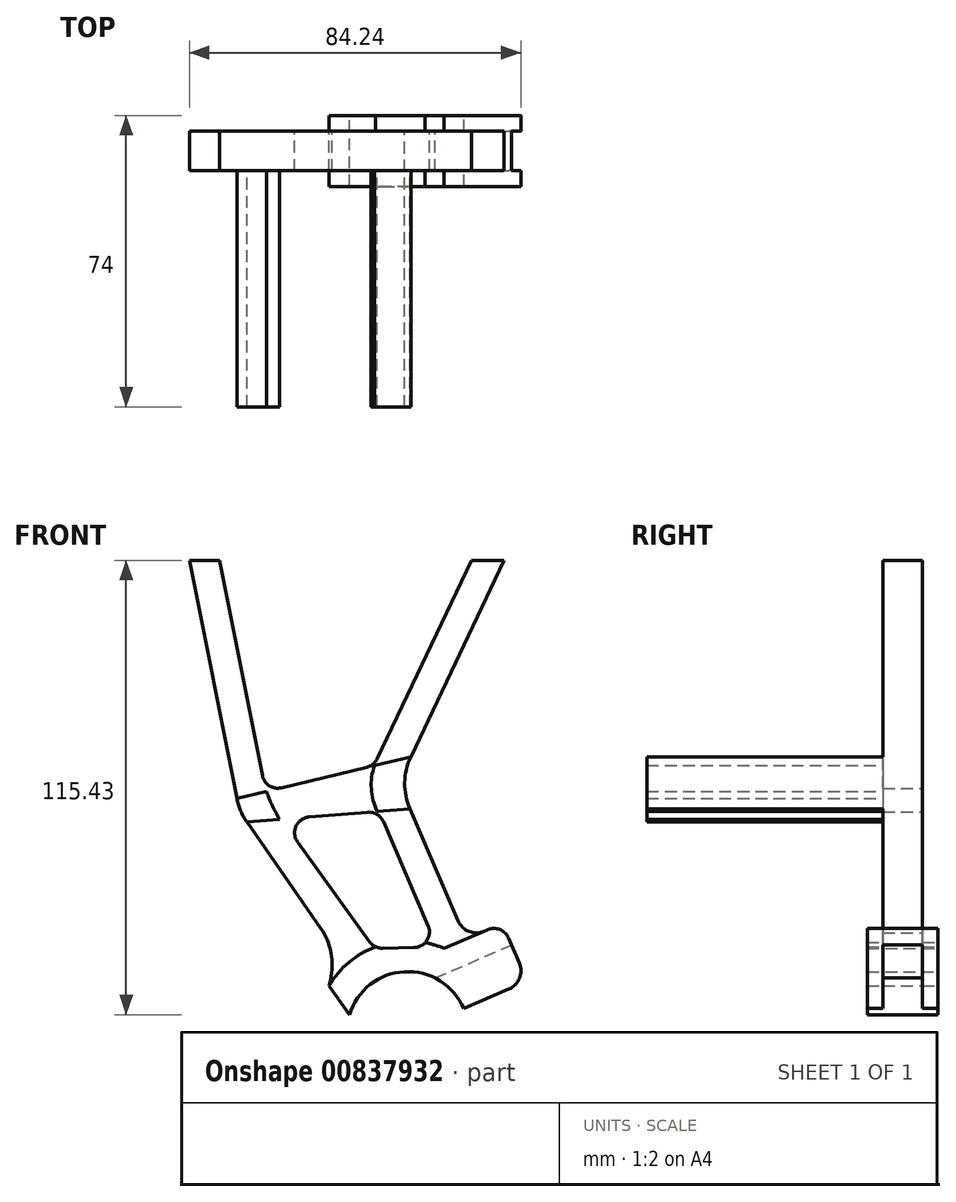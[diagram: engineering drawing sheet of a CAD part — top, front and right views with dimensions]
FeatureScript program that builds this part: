
annotation { "Feature Type Name" : "Feature", "Feature Type Description" : "" }
export const myFeature = defineFeature(function(context is Context, id is Id, definition is map)
    precondition{}
    {
        {
            var Q0;
            Q0=qCreatedBy(makeId("Front.planeOp"),FACE);
            var sketch = newSketch(context, id + "F0", { "sketchPlane" : qUnion([Q0])});
            skCircle(sketch, "E0", {"center": v(15.5, -66) * mm, "radius": 15.5 * mm});
            skLineSegment(sketch, "E1.bottom", {"start": v(-80, 54) * mm, "end": v(80, 54) * mm});
            skLineSegment(sketch, "E1.top", {"start": v(-80, 60) * mm, "end": v(80, 60) * mm});
            skLineSegment(sketch, "E1.left", {"start": v(-80, 54) * mm, "end": v(-80, 60) * mm});
            skLineSegment(sketch, "E1.right", {"start": v(80, 54) * mm, "end": v(80, 60) * mm});
            skLineSegment(sketch, "E2", {"start": v(-40, 54) * mm, "end": v(-27.92, -6.51) * mm});
            skCircle(sketch, "E3", {"center": v(15.5, -66) * mm, "radius": 23 * mm});
            skLineSegment(sketch, "E4", {"start": v(-25.36, -12.5) * mm, "end": v(-6.56, -39.57) * mm});
            skLineSegment(sketch, "E5", {"start": v(40, 54) * mm, "end": v(16.28, 4.1) * mm});
            skLineSegment(sketch, "E6", {"start": v(16.03, -9.1) * mm, "end": v(36.62, -56.9) * mm});
            skPoint(sketch, "E7.visualSharp", {"position": v(13.17, -2.45) * mm});
            skArc(sketch, "E7.filletArc", {"start": v(16.28, 4.1) * mm, "mid": v(14.73, -2.48) * mm, "end": v(16.03, -9.1) * mm});
            skPoint(sketch, "E8.visualSharp", {"position": v(-27.26, -9.77) * mm});
            skArc(sketch, "E8.filletArc", {"start": v(-27.92, -6.51) * mm, "mid": v(-26.95, -9.64) * mm, "end": v(-25.36, -12.5) * mm});
            skLineSegment(sketch, "E9", {"start": v(-16.58, -3.79) * mm, "end": v(5.05, 1.4) * mm});
            skLineSegment(sketch, "E10", {"start": v(-9.57, -11.2) * mm, "end": v(5.28, -9.99) * mm});
            skLineSegment(sketch, "E11", {"start": v(-32.35, 54) * mm, "end": v(-21.43, -0.68) * mm});
            skLineSegment(sketch, "E12", {"start": v(-12.49, -17.54) * mm, "end": v(5.82, -42.9) * mm});
            skLineSegment(sketch, "E13", {"start": v(31.7, 54) * mm, "end": v(7.73, 3.57) * mm});
            skLineSegment(sketch, "E14", {"start": v(9.28, -12.4) * mm, "end": v(20.66, -38.8) * mm});
            skArc(sketch, "E15.filletArc", {"start": v(-9.57, -11.2) * mm, "mid": v(-12.88, -13.52) * mm, "end": v(-12.49, -17.54) * mm});
            skArc(sketch, "E16.filletArc", {"start": v(9.28, -12.4) * mm, "mid": v(7.67, -10.55) * mm, "end": v(5.28, -9.99) * mm});
            skArc(sketch, "E17.filletArc", {"start": v(5.05, 1.4) * mm, "mid": v(6.63, 2.18) * mm, "end": v(7.73, 3.57) * mm});
            skArc(sketch, "E18.filletArc", {"start": v(-21.43, -0.68) * mm, "mid": v(-19.66, -3.27) * mm, "end": v(-16.58, -3.79) * mm});
            skLineSegment(sketch, "E19", {"start": v(9.15, -44.56) * mm, "end": v(17.08, -44.4) * mm});
            skPoint(sketch, "E20.visualSharp", {"position": v(7.05, -44.6) * mm});
            skArc(sketch, "E20.filletArc", {"start": v(5.82, -42.9) * mm, "mid": v(7.28, -44.15) * mm, "end": v(9.15, -44.56) * mm});
            skPoint(sketch, "E21.visualSharp", {"position": v(23.01, -44.26) * mm});
            skArc(sketch, "E21.filletArc", {"start": v(17.08, -44.4) * mm, "mid": v(20.36, -42.55) * mm, "end": v(20.66, -38.8) * mm});
            skLineSegment(sketch, "E22", {"start": v(2.52, -63.97) * mm, "end": v(-12.93, -42.55) * mm});
            skPoint(sketch, "E22.endSnap0", {"position": v(20.36, -42.55) * mm});
            skLineSegment(sketch, "E23", {"start": v(-8.28, -49) * mm, "end": v(3.89, -40.23) * mm});
            skLineSegment(sketch, "E24", {"start": v(-7.5, -66) * mm, "end": v(-4.16, -52.56) * mm});
            skPoint(sketch, "E25.newPointA", {"position": v(-2.2, -44.62) * mm});
            skPoint(sketch, "E25.newPointB", {"position": v(0, -49) * mm});
            skArc(sketch, "E25.filletArc", {"start": v(-4.16, -52.56) * mm, "mid": v(-3.96, -45.8) * mm, "end": v(-6.56, -39.57) * mm});
            skLineSegment(sketch, "E26", {"start": v(15.5, -66) * mm, "end": v(36.62, -56.9) * mm});
            skLineSegment(sketch, "E27", {"start": v(36.62, -56.9) * mm, "end": v(45.8, -52.94) * mm});
            skLineSegment(sketch, "E28", {"start": v(45.8, -52.94) * mm, "end": v(39.48, -38.25) * mm});
            skLineSegment(sketch, "E29", {"start": v(39.48, -38.25) * mm, "end": v(-3.82, -56.9) * mm});
            skSolve(sketch);
        }
        {
            var Q0;
            {var subQ5=sQuery(id+"F0.wireOp",EDGE,"E2");Q0=makeQuery(id+"F0.imprint","IMPRINT",FACE,{"disambiguationData":[TD([[makeQuery(id+"F0.imprint","IMPRINT",EDGE,{"derivedFrom":subQ5}),1.0]])]});}
            var Q1;
            {var subQ9=sQuery(id+"F0.wireOp",EDGE,"E19");Q1=makeQuery(id+"F0.imprint","IMPRINT",FACE,{"disambiguationData":[TD([[makeQuery(id+"F0.imprint","IMPRINT",EDGE,{"derivedFrom":subQ9}),-1.0]])]});}
            var Q2;
            {var subQ3=sQuery(id+"F0.wireOp",EDGE,"E3");var subQ5=sQuery(id+"F0.wireOp",EDGE,"E20.filletArc");var subQ8=makeQuery(id+"F0.imprint","INTERSECT",VERTEX,{"derivedFrom":[subQ3,subQ5]});Q2=makeQuery(id+"F0.imprint","IMPRINT",FACE,{"disambiguationData":[TD([[makeQuery(id+"F0.imprint","IMPRINT",EDGE,{"disambiguationData":[TD([[subQ8,-1.0]])],"derivedFrom":subQ3}),-1.0]])]});}
            var Q3;
            {var subQ0=sQuery(id+"F0.wireOp",EDGE,"E27");Q3=makeQuery(id+"F0.imprint","IMPRINT",FACE,{"disambiguationData":[TD([[makeQuery(id+"F0.imprint","IMPRINT",EDGE,{"derivedFrom":subQ0}),1.0]])]});}
            var Q4;
            {var subQ0=sQuery(id+"F0.wireOp",EDGE,"E29");var subQ1=sQuery(id+"F0.wireOp",EDGE,"E0");var subQ2=makeQuery(id+"F0.imprint","INTERSECT",VERTEX,{"derivedFrom":[subQ1,subQ0]});Q4=makeQuery(id+"F0.imprint","IMPRINT",FACE,{"disambiguationData":[TD([[makeQuery(id+"F0.imprint","IMPRINT",EDGE,{"disambiguationData":[TD([[subQ2,1.0]])],"derivedFrom":subQ1}),-1.0]])]});}
            var Q5;
            {var subQ0=sQuery(id+"F0.wireOp",EDGE,"E6");var subQ3=sQuery(id+"F0.wireOp",EDGE,"E29");var subQ5=makeQuery(id+"F0.imprint","INTERSECT",VERTEX,{"derivedFrom":[subQ0,subQ3]});Q5=makeQuery(id+"F0.imprint","IMPRINT",FACE,{"disambiguationData":[TD([[makeQuery(id+"F0.imprint","IMPRINT",EDGE,{"disambiguationData":[TD([[subQ5,-1.0]])],"derivedFrom":subQ3}),1.0]])]});}
            extrude(context, id + "F1", {"entities" : qUnion([Q0, Q1, Q2, Q3, Q4, Q5]), "depth" : 10 * mm, "offsetDistance" : 25 * mm});
        }
        {
            var Q0;
            Q0=makeQuery(id+"F1.opExtrude","CAP_FACE",FACE,{"disambiguationData":[OSD([sQuery(id+"F0.wireOp",EDGE,"E0"),sQuery(id+"F0.wireOp",EDGE,"E1.bottom"),sQuery(id+"F0.wireOp",EDGE,"E2"),sQuery(id+"F0.wireOp",EDGE,"E4"),sQuery(id+"F0.wireOp",EDGE,"E5"),sQuery(id+"F0.wireOp",EDGE,"E6"),sQuery(id+"F0.wireOp",EDGE,"E7.filletArc"),sQuery(id+"F0.wireOp",EDGE,"E8.filletArc"),sQuery(id+"F0.wireOp",EDGE,"E9"),sQuery(id+"F0.wireOp",EDGE,"E10"),sQuery(id+"F0.wireOp",EDGE,"E11"),sQuery(id+"F0.wireOp",EDGE,"E12"),sQuery(id+"F0.wireOp",EDGE,"E13"),sQuery(id+"F0.wireOp",EDGE,"E14"),sQuery(id+"F0.wireOp",EDGE,"E15.filletArc"),sQuery(id+"F0.wireOp",EDGE,"E16.filletArc"),sQuery(id+"F0.wireOp",EDGE,"E17.filletArc"),sQuery(id+"F0.wireOp",EDGE,"E18.filletArc"),sQuery(id+"F0.wireOp",EDGE,"E19"),sQuery(id+"F0.wireOp",EDGE,"E20.filletArc"),sQuery(id+"F0.wireOp",EDGE,"E21.filletArc"),sQuery(id+"F0.wireOp",EDGE,"E22"),sQuery(id+"F0.wireOp",EDGE,"E24"),sQuery(id+"F0.wireOp",EDGE,"E25.filletArc"),sQuery(id+"F0.wireOp",EDGE,"E26"),sQuery(id+"F0.wireOp",EDGE,"E27"),sQuery(id+"F0.wireOp",EDGE,"E28"),sQuery(id+"F0.wireOp",EDGE,"E29")])],"isStart":false});
            var sketch = newSketch(context, id + "F2", { "sketchPlane" : qUnion([Q0])});
            skLineSegment(sketch, "E30", {"start": v(39.48, -38.25) * mm, "end": v(45.8, -52.94) * mm});
            skLineSegment(sketch, "E31", {"start": v(45.8, -52.94) * mm, "end": v(29.74, -59.87) * mm});
            skArc(sketch, "E32", {"start": v(29.74, -59.87) * mm, "mid": v(14.67, -50.52) * mm, "end": v(0.69, -61.43) * mm});
            skCircle(sketch, "E33", {"center": v(15.5, -66) * mm, "radius": 23.3 * mm});
            skLineSegment(sketch, "E34", {"start": v(0.69, -61.43) * mm, "end": v(-4.56, -54.16) * mm});
            skLineSegment(sketch, "E35", {"start": v(39.48, -38.25) * mm, "end": v(24.72, -44.6) * mm});
            skSolve(sketch);
        }
        {
            var Q0;
            {var subQ6=sQuery(id+"F2.wireOp",EDGE,"E32");Q0=makeQuery(id+"F2.imprint","IMPRINT",FACE,{"disambiguationData":[TD([[makeQuery(id+"F2.imprint","IMPRINT",EDGE,{"derivedFrom":subQ6}),-1.0]])]});}
            var Q1;
            {var subQ5=sQuery(id+"F2.wireOp",EDGE,"E30");Q1=makeQuery(id+"F2.imprint","IMPRINT",FACE,{"disambiguationData":[TD([[makeQuery(id+"F2.imprint","IMPRINT",EDGE,{"derivedFrom":subQ5}),1.0]])]});}
            extrude(context, id + "F3", {"entities" : qUnion([Q0, Q1]), "operationType" : NewBodyOperationType.ADD, "depth" : 4 * mm, "offsetDistance" : 25 * mm, "hasSecondDirection" : true, "secondDirectionOppositeDirection" : true, "secondDirectionDepth" : 14 * mm});
        }
        {
            var Q0;
            Q0=makeQuery(id+"F3.boolean.opBoolean","MERGE",FACE,{"derivedFrom":[makeQuery(id+"F1.opExtrude","SWEPT_FACE",FACE,{"disambiguationData":[OSD([sQuery(id+"F0.wireOp",EDGE,"E28")])]}),makeQuery(id+"F3.opExtrude","SWEPT_FACE",FACE,{"disambiguationData":[OSD([sQuery(id+"F2.wireOp",EDGE,"E30")])]})]});
            var sketch = newSketch(context, id + "F4", { "sketchPlane" : qUnion([Q0])});
            skLineSegment(sketch, "E36.bottom", {"start": v(-10, -66.75) * mm, "end": v(0, -66.75) * mm});
            skLineSegment(sketch, "E36.top", {"start": v(-10, -56.75) * mm, "end": v(0, -56.75) * mm});
            skLineSegment(sketch, "E36.left", {"start": v(-10, -66.75) * mm, "end": v(-10, -56.75) * mm});
            skLineSegment(sketch, "E36.right", {"start": v(0, -66.75) * mm, "end": v(0, -56.75) * mm});
            skSolve(sketch);
        }
        {
            var Q0;
            Q0=makeQuery(id+"F4.imprint","IMPRINT",FACE,{"disambiguationData":[TD([[makeQuery(id+"F4.imprint","IMPRINT",EDGE,{"derivedFrom":sQuery(id+"F4.wireOp",EDGE,"E36.bottom")}),1.0]])]});
            extrude(context, id + "F5", {"entities" : qUnion([Q0]), "operationType" : NewBodyOperationType.REMOVE, "oppositeDirection" : true, "depth" : 25 * mm, "offsetDistance" : 25 * mm});
        }
        {
            var Q0;
            Q0=makeQuery(id+"F1.opExtrude","SWEPT_EDGE",EDGE,{"disambiguationData":[OSD([sQuery(id+"F0.wireOp",EDGE,"E6"),sQuery(id+"F0.wireOp",EDGE,"E29")])]});
            fillet(context, id + "F6", {"entities" : qUnion([Q0]), "radius" : 5 * mm, "tangentPropagation" : true, "allowEdgeOverflow" : false});
        }
        {
            var Q0;
            Q0=makeQuery(id+"F3.boolean.opBoolean","MERGE",EDGE,{"derivedFrom":[makeQuery(id+"F1.opExtrude","SWEPT_EDGE",EDGE,{"disambiguationData":[OSD([sQuery(id+"F0.wireOp",EDGE,"E28"),sQuery(id+"F0.wireOp",EDGE,"E29")])]}),makeQuery(id+"F3.opExtrude","SWEPT_EDGE",EDGE,{"disambiguationData":[OSD([sQuery(id+"F2.wireOp",EDGE,"E30"),sQuery(id+"F2.wireOp",EDGE,"E35")])]})]});
            fillet(context, id + "F7", {"entities" : qUnion([Q0]), "radius" : 4 * mm, "tangentPropagation" : true, "allowEdgeOverflow" : false});
        }
        {
            var Q0;
            {var subQ0=sQuery(id+"F2.wireOp",EDGE,"E31");var subQ1=sQuery(id+"F2.wireOp",EDGE,"E30");var subQ2=sQuery(id+"F0.wireOp",EDGE,"E28");var subQ3=sQuery(id+"F0.wireOp",EDGE,"E27");Q0=makeQuery(id+"F5.boolean.opBoolean","SPLIT",EDGE,{"disambiguationData":[TD([makeQuery(id+"F5.opExtrude","SWEPT_FACE",FACE,{"disambiguationData":[OSD([sQuery(id+"F4.wireOp",EDGE,"E36.left")])]})])],"derivedFrom":makeQuery(id+"F3.boolean.opBoolean","MERGE",EDGE,{"derivedFrom":[makeQuery(id+"F1.opExtrude","SWEPT_EDGE",EDGE,{"disambiguationData":[OSD([subQ3,subQ2])]}),makeQuery(id+"F3.opExtrude","SWEPT_EDGE",EDGE,{"disambiguationData":[OSD([subQ1,subQ0])]})]})});}
            var Q1;
            {var subQ0=sQuery(id+"F2.wireOp",EDGE,"E31");var subQ1=sQuery(id+"F2.wireOp",EDGE,"E30");var subQ2=sQuery(id+"F0.wireOp",EDGE,"E28");var subQ3=sQuery(id+"F0.wireOp",EDGE,"E27");Q1=makeQuery(id+"F5.boolean.opBoolean","SPLIT",EDGE,{"disambiguationData":[TD([makeQuery(id+"F5.opExtrude","SWEPT_FACE",FACE,{"disambiguationData":[OSD([sQuery(id+"F4.wireOp",EDGE,"E36.right")])]})])],"derivedFrom":makeQuery(id+"F3.boolean.opBoolean","MERGE",EDGE,{"derivedFrom":[makeQuery(id+"F1.opExtrude","SWEPT_EDGE",EDGE,{"disambiguationData":[OSD([subQ3,subQ2])]}),makeQuery(id+"F3.opExtrude","SWEPT_EDGE",EDGE,{"disambiguationData":[OSD([subQ1,subQ0])]})]})});}
            fillet(context, id + "F8", {"entities" : qUnion([Q0, Q1]), "radius" : 5 * mm, "tangentPropagation" : true, "allowEdgeOverflow" : false});
        }
        {
            var Q0;
            Q0=makeQuery(id+"F1.opExtrude","CAP_FACE",FACE,{"disambiguationData":[OSD([sQuery(id+"F0.wireOp",EDGE,"E0"),sQuery(id+"F0.wireOp",EDGE,"E1.bottom"),sQuery(id+"F0.wireOp",EDGE,"E2"),sQuery(id+"F0.wireOp",EDGE,"E4"),sQuery(id+"F0.wireOp",EDGE,"E5"),sQuery(id+"F0.wireOp",EDGE,"E6"),sQuery(id+"F0.wireOp",EDGE,"E7.filletArc"),sQuery(id+"F0.wireOp",EDGE,"E8.filletArc"),sQuery(id+"F0.wireOp",EDGE,"E9"),sQuery(id+"F0.wireOp",EDGE,"E10"),sQuery(id+"F0.wireOp",EDGE,"E11"),sQuery(id+"F0.wireOp",EDGE,"E12"),sQuery(id+"F0.wireOp",EDGE,"E13"),sQuery(id+"F0.wireOp",EDGE,"E14"),sQuery(id+"F0.wireOp",EDGE,"E15.filletArc"),sQuery(id+"F0.wireOp",EDGE,"E16.filletArc"),sQuery(id+"F0.wireOp",EDGE,"E17.filletArc"),sQuery(id+"F0.wireOp",EDGE,"E18.filletArc"),sQuery(id+"F0.wireOp",EDGE,"E19"),sQuery(id+"F0.wireOp",EDGE,"E20.filletArc"),sQuery(id+"F0.wireOp",EDGE,"E21.filletArc"),sQuery(id+"F0.wireOp",EDGE,"E22"),sQuery(id+"F0.wireOp",EDGE,"E24"),sQuery(id+"F0.wireOp",EDGE,"E25.filletArc"),sQuery(id+"F0.wireOp",EDGE,"E26"),sQuery(id+"F0.wireOp",EDGE,"E27"),sQuery(id+"F0.wireOp",EDGE,"E28"),sQuery(id+"F0.wireOp",EDGE,"E29")])],"isStart":false});
            var sketch = newSketch(context, id + "F9", { "sketchPlane" : qUnion([Q0])});
            skLineSegment(sketch, "E37", {"start": v(5.05, 1.4) * mm, "end": v(-16.58, -3.79) * mm});
            skLineSegment(sketch, "E38", {"start": v(-16.58, -3.79) * mm, "end": v(-27.92, -6.51) * mm});
            skLineSegment(sketch, "E39", {"start": v(5.05, 1.4) * mm, "end": v(16.28, 4.1) * mm});
            skLineSegment(sketch, "E40", {"start": v(-9.57, -11.2) * mm, "end": v(5.28, -9.99) * mm});
            skLineSegment(sketch, "E41", {"start": v(5.28, -9.99) * mm, "end": v(16.03, -9.1) * mm});
            skLineSegment(sketch, "E42", {"start": v(-9.57, -11.2) * mm, "end": v(-25.36, -12.5) * mm});
            skArc(sketch, "E43", {"start": v(-27.92, -6.51) * mm, "mid": v(-26.95, -9.64) * mm, "end": v(-25.36, -12.5) * mm});
            skArc(sketch, "E44", {"start": v(16.28, 4.1) * mm, "mid": v(14.73, -2.48) * mm, "end": v(16.03, -9.1) * mm});
            skArc(sketch, "E45", {"start": v(7.73, 3.57) * mm, "mid": v(6.3, -4.63) * mm, "end": v(9.28, -12.4) * mm});
            skArc(sketch, "E46", {"start": v(-21.43, -0.68) * mm, "mid": v(-18.2, -9.76) * mm, "end": v(-12.49, -17.54) * mm});
            skSolve(sketch);
        }
        {
            var Q0;
            {var subQ0=sQuery(id+"F9.wireOp",EDGE,"E43");Q0=makeQuery(id+"F9.imprint","IMPRINT",FACE,{"disambiguationData":[TD([[makeQuery(id+"F9.imprint","IMPRINT",EDGE,{"derivedFrom":subQ0}),1.0]])]});}
            var Q1;
            {var subQ0=sQuery(id+"F9.wireOp",EDGE,"E44");Q1=makeQuery(id+"F9.imprint","IMPRINT",FACE,{"disambiguationData":[TD([[makeQuery(id+"F9.imprint","IMPRINT",EDGE,{"derivedFrom":subQ0}),-1.0]])]});}
            extrude(context, id + "F10", {"entities" : qUnion([Q0, Q1]), "operationType" : NewBodyOperationType.ADD, "depth" : 60 * mm, "offsetDistance" : 25 * mm});
        }
    });
